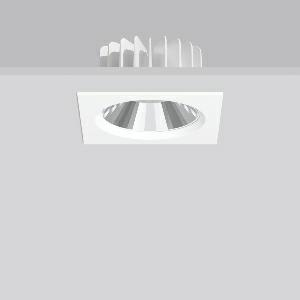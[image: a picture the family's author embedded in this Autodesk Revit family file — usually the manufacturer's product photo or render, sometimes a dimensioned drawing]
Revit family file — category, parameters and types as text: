
# Revit family: ledona_square_ip20_901796_002_5b99
name_source: partatom
category: Lighting Fixtures
units: mm (PartAtom-declared; Revit-internal decimal feet)

## family parameters
Cut with Voids When Loaded = No
Host = Face
Light Source = No
Part Type = Normal
Room Calculation Point = No
Round Connector Dimension = Use Diameter
Shared = No

## types (1)
- MultiLumen 1 (1 x LED Modul 930, 1650 lm, 3000)
    Apparent Load = 12 VA
    Approval mark = CE
    CIE Flux Codes = 91 100 100 100 100
    Color Rendering = 90
    Color Temperature = 3000
    Default Elevation = 1800 mm
    Description = Series: LEDONA square
Recessed LED downlight featuring advanced technology and sophisticated design. Housing: die-cast aluminium constructed as heat sink. Square cover plate: die-cast aluminium, powder coated. Round ceiling cut-out also with square types. MultiLumen: Luminous flux adjustable in different steps. Best colour rendering index Ra>90. Installation without tools thanks to spring fastening system. Connected converter included in separate gearbox. With connecting cable (L 250 mm). Suitable for through-wiring with separately available accessories. Through-wiring box (5 pole) available as accessory. 
Colour: white
Length: 170 mm
Width: 170 mm
Height: 3 mm
Cut-out diameter: 160 mm
Recess height: 89 mm
Luminaire: recess height: 89 mm
Lamp: LED
Socket: without socket
Colour temperature: 3000K
Colour rendering index (CRI): 92
System power: 12 W
Rated luminous flux: 1650 lm
Luminous efficiency: 138 lm/W
System power 2: 19 W
Rated luminous flux 2: 2550 lm
Luminous efficiency 2: 134 lm/W
System power 3: 27 W
Rated luminous flux 3: 3450 lm
Luminous efficiency 3: 128 lm/W
System power 4: 39 W
Rated luminous flux 4: 4600 lm
Luminous efficiency 4: 118 lm/W
Control gear: Regulated power supply
Protection class: II
Type of protection: IP 20
    Height = 0 mm  [stored 0 ft]
    Lamp = 1 x LED Modul 930
    Lamp Light Flux = 1650 lm
    Lamp count = 1
    Length = 170 mm  [stored 0.557743 ft]
    Lifetime = 50000 h
    Luminous efficacy = 138 lm/W
    Manufacturer = RZB
    ModVariant = No
    Model = 901796.002
    Mounting Place = Ceiling
    Mounting Type = Recessed
    Number of Poles = 1
    OnlyDefault = Yes
    Power Factor = 1
    Product Name = LEDONA square IP20
    Product group = Recessed downlights
    ProductGroupID = 402
    Protection Class = Protection class II
    Protection Degree = IP 20
    RLX_Detail_Level = 1
    RLX_Emergency_Light_Flux = 0 lm
    RLX_Emergency_Type = 0
    RLX_Emergency_Type_DB = No
    RlxData = <blob elided: 33601 chars, md5=a4a616ab>
    Socket = socket
    Standby Power = 0 W
    System Light Flux = 1650 lm
    System Power = 12 W
    Type Comments = MultiLumen 1
    Type Image = 901391.002.jpg
    URL = http://relux.com
    VarID = multilumen_1
    Voltage = 230 V
    Voltage Range = 220-240 V
    Weight = 0.00 kg
    Width = 170 mm  [stored 0.557743 ft]

note: [stored X ft] marks values corroborated as IEEE doubles in the binary element streams (Revit-internal decimal feet)

## geometry (parser evidence)
native form markers: Blend x4, Sweep x8
no freeform markers — native parametric forms only
